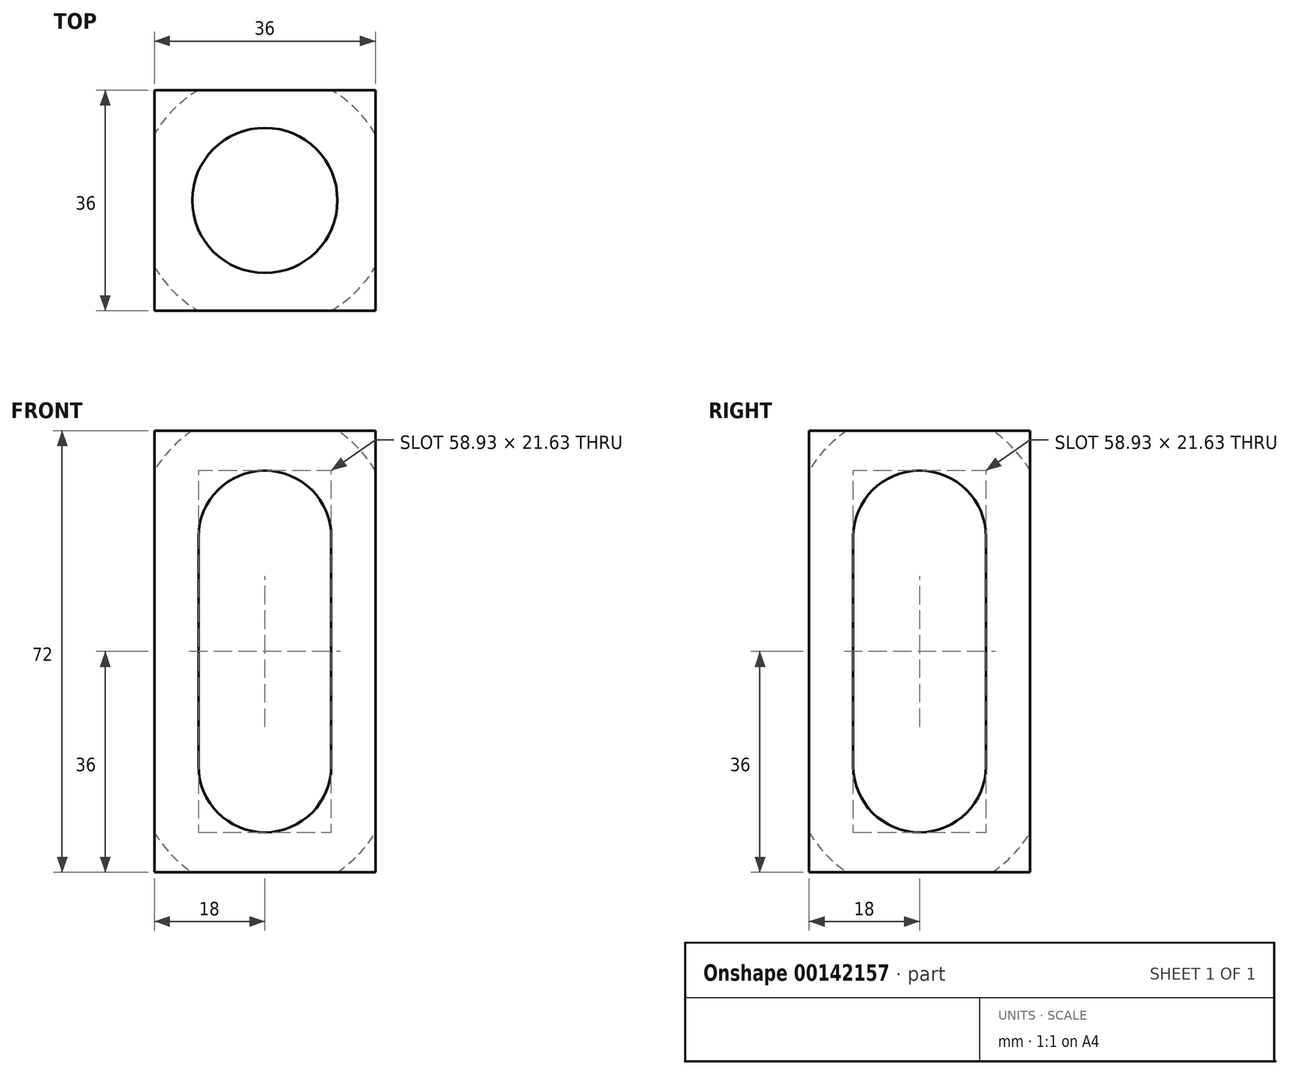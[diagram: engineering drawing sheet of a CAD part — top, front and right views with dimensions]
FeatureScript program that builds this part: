
annotation { "Feature Type Name" : "Feature", "Feature Type Description" : "" }
export const myFeature = defineFeature(function(context is Context, id is Id, definition is map)
    precondition{}
    {
        {
            var Q0;
            Q0=qCreatedBy(makeId("Front.planeOp"),FACE);
            var sketch = newSketch(context, id + "F0", { "sketchPlane" : qUnion([Q0])});
            skLineSegment(sketch, "E0", {"start": v(-126.35, 0) * mm, "end": v(133.97, 0) * mm, "construction": true});
            skLineSegment(sketch, "E1", {"start": v(0, -94.48) * mm, "end": v(0, 84.32) * mm});
            skLineSegment(sketch, "E2.bottom", {"start": v(-18, 36) * mm, "end": v(18, 36) * mm});
            skLineSegment(sketch, "E2.top", {"start": v(-18, -36) * mm, "end": v(18, -36) * mm});
            skLineSegment(sketch, "E2.left", {"start": v(-18, 36) * mm, "end": v(-18, -36) * mm});
            skLineSegment(sketch, "E2.right", {"start": v(18, 36) * mm, "end": v(18, -36) * mm});
            skArc(sketch, "E3", {"start": v(21, 18.65) * mm, "mid": v(0, 39.65) * mm, "end": v(-21, 18.65) * mm});
            skArc(sketch, "E4", {"start": v(-21, -18.65) * mm, "mid": v(0, -39.65) * mm, "end": v(21, -18.65) * mm});
            skLineSegment(sketch, "E5", {"start": v(-21, 18.65) * mm, "end": v(-21, -18.65) * mm});
            skLineSegment(sketch, "E6", {"start": v(21, 18.65) * mm, "end": v(21, -18.65) * mm});
            skSolve(sketch);
        }
        {
            var Q0;
            {var subQ0=sQuery(id+"F0.wireOp",EDGE,"E2.left");var subQ1=sQuery(id+"F0.wireOp",EDGE,"E2.bottom");var subQ2=makeQuery(id+"F0.imprint","INTERSECT",VERTEX,{"derivedFrom":[subQ1,subQ0]});Q0=makeQuery(id+"F0.imprint","IMPRINT",FACE,{"disambiguationData":[TD([[makeQuery(id+"F0.imprint","IMPRINT",EDGE,{"disambiguationData":[TD([[subQ2,-1.0]])],"derivedFrom":subQ1}),-1.0]])]});}
            var Q1;
            {var subQ0=sQuery(id+"F0.wireOp",EDGE,"E3");var subQ11=sQuery(id+"F0.wireOp",EDGE,"E2.bottom");var subQ12=makeQuery(id+"F0.imprint","INTERSECT",VERTEX,{"disambiguationData":[OD(0.0)],"derivedFrom":[subQ11,subQ0]});Q1=makeQuery(id+"F0.imprint","IMPRINT",FACE,{"disambiguationData":[TD([[makeQuery(id+"F0.imprint","IMPRINT",EDGE,{"disambiguationData":[TD([[subQ12,-1.0]])],"derivedFrom":subQ11}),-1.0]])]});}
            var Q2;
            {var subQ0=sQuery(id+"F0.wireOp",EDGE,"E2.right");var subQ1=sQuery(id+"F0.wireOp",EDGE,"E2.bottom");var subQ2=makeQuery(id+"F0.imprint","INTERSECT",VERTEX,{"derivedFrom":[subQ1,subQ0]});Q2=makeQuery(id+"F0.imprint","IMPRINT",FACE,{"disambiguationData":[TD([[makeQuery(id+"F0.imprint","IMPRINT",EDGE,{"disambiguationData":[TD([[subQ2,1.0]])],"derivedFrom":subQ1}),-1.0]])]});}
            var Q3;
            {var subQ0=sQuery(id+"F0.wireOp",EDGE,"E2.left");var subQ1=sQuery(id+"F0.wireOp",EDGE,"E2.top");var subQ2=makeQuery(id+"F0.imprint","INTERSECT",VERTEX,{"derivedFrom":[subQ1,subQ0]});Q3=makeQuery(id+"F0.imprint","IMPRINT",FACE,{"disambiguationData":[TD([[makeQuery(id+"F0.imprint","IMPRINT",EDGE,{"disambiguationData":[TD([[subQ2,-1.0]])],"derivedFrom":subQ1}),1.0]])]});}
            var Q4;
            {var subQ0=sQuery(id+"F0.wireOp",EDGE,"E2.right");var subQ1=sQuery(id+"F0.wireOp",EDGE,"E2.top");var subQ2=makeQuery(id+"F0.imprint","INTERSECT",VERTEX,{"derivedFrom":[subQ1,subQ0]});Q4=makeQuery(id+"F0.imprint","IMPRINT",FACE,{"disambiguationData":[TD([[makeQuery(id+"F0.imprint","IMPRINT",EDGE,{"disambiguationData":[TD([[subQ2,1.0]])],"derivedFrom":subQ1}),1.0]])]});}
            var Q5;
            {var subQ5=sQuery(id+"F0.wireOp",EDGE,"E2.top");var subQ7=sQuery(id+"F0.wireOp",EDGE,"E1");var subQ8=makeQuery(id+"F0.imprint","INTERSECT",VERTEX,{"derivedFrom":[subQ7,subQ5]});Q5=makeQuery(id+"F0.imprint","IMPRINT",FACE,{"disambiguationData":[TD([[makeQuery(id+"F0.imprint","IMPRINT",EDGE,{"disambiguationData":[TD([[subQ8,-1.0]])],"derivedFrom":subQ7}),-1.0]])]});}
            extrude(context, id + "F1", {"entities" : qUnion([Q0, Q1, Q2, Q3, Q4, Q5]), "endBound" : BoundingType.SYMMETRIC, "depth" : 36 * mm});
        }
        {
            var Q0;
            {var subQ5=sQuery(id+"F0.wireOp",EDGE,"E5");Q0=makeQuery(id+"F0.imprint","IMPRINT",FACE,{"disambiguationData":[TD([[makeQuery(id+"F0.imprint","IMPRINT",EDGE,{"derivedFrom":subQ5}),1.0]])]});}
            var Q1;
            {var subQ0=sQuery(id+"F0.wireOp",EDGE,"E3");var subQ11=sQuery(id+"F0.wireOp",EDGE,"E2.bottom");var subQ12=makeQuery(id+"F0.imprint","INTERSECT",VERTEX,{"disambiguationData":[OD(0.0)],"derivedFrom":[subQ11,subQ0]});Q1=makeQuery(id+"F0.imprint","IMPRINT",FACE,{"disambiguationData":[TD([[makeQuery(id+"F0.imprint","IMPRINT",EDGE,{"disambiguationData":[TD([[subQ12,-1.0]])],"derivedFrom":subQ11}),-1.0]])]});}
            var Q2;
            {var subQ5=sQuery(id+"F0.wireOp",EDGE,"E6");Q2=makeQuery(id+"F0.imprint","IMPRINT",FACE,{"disambiguationData":[TD([[makeQuery(id+"F0.imprint","IMPRINT",EDGE,{"derivedFrom":subQ5}),-1.0]])]});}
            var Q3;
            {var subQ0=sQuery(id+"F0.wireOp",EDGE,"E3");var subQ1=sQuery(id+"F0.wireOp",EDGE,"E2.bottom");var subQ2=makeQuery(id+"F0.imprint","INTERSECT",VERTEX,{"disambiguationData":[OD(0.0)],"derivedFrom":[subQ1,subQ0]});Q3=makeQuery(id+"F0.imprint","IMPRINT",FACE,{"disambiguationData":[TD([[makeQuery(id+"F0.imprint","IMPRINT",EDGE,{"disambiguationData":[TD([[subQ2,-1.0]])],"derivedFrom":subQ1}),1.0]])]});}
            var Q4;
            {var subQ0=sQuery(id+"F0.wireOp",EDGE,"E4");var subQ1=sQuery(id+"F0.wireOp",EDGE,"E2.top");var subQ2=makeQuery(id+"F0.imprint","INTERSECT",VERTEX,{"disambiguationData":[OD(0.0)],"derivedFrom":[subQ1,subQ0]});Q4=makeQuery(id+"F0.imprint","IMPRINT",FACE,{"disambiguationData":[TD([[makeQuery(id+"F0.imprint","IMPRINT",EDGE,{"disambiguationData":[TD([[subQ2,-1.0]])],"derivedFrom":subQ1}),-1.0]])]});}
            var Q5;
            Q5=sQuery(id+"F0.wireOp",EDGE,"E1");
            revolve(context, id + "F2", {"operationType" : NewBodyOperationType.REMOVE, "entities" : qUnion([Q0, Q1, Q2, Q3, Q4]), "axis" : qUnion([Q5]), "revolveType" : RevolveType.FULL, "oppositeDirection" : true});
        }
    });
